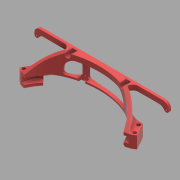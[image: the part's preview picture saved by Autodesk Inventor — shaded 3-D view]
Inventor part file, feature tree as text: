
AUTODESK INVENTOR PART (.ipt)
format: ipt  version: 2017 (Build 210142000, 142)  size: 909,824 bytes
history: native  units: mm
features: sketch x17, extrude x13, projected_geometry x12, other x8, fillet x8, plane x5, hole x4, chamfer x3, reference x3, mirror x2
ambient origin geometry x8: Origin, YZ Plane, XZ Plane, XY Plane, X Axis, Y Axis, Z Axis, Center Point
bodies: Body1 (feature_tree), Body2 (feature_tree), Body3 (feature_tree)
feature tree (75):
  other  "core"
  extrude  "Extrusion1"  Depth=12.0mm
  extrude  "Extrusion2"  Depth=18.0mm
  extrude  "Extrusion3"  Depth=17.453293mm
  chamfer  "Chamfer1"  Distance=5.0mm
  hole  "Hole1"  [1 undecoded]
  hole  "Hole2"  [1 undecoded]
  plane  "Work Plane1"
  extrude  "Extrusion4"  Depth=4.0mm
  extrude  "Extrusion5"  Depth=24.0mm TaperAngle=0.0deg
  extrude  "Extrusion6"  Depth=10.0mm
  extrude  "Extrusion11"  Depth=4.0mm TaperAngle=0.0deg
  mirror  "Mirror1"
  extrude  "Extrusion13"  Depth=0.65mm TaperAngle=45.0deg
  chamfer  "Chamfer4"  Distance=0.65mm
  plane  "Work Plane3"
  mirror  "Mirror2"
  fillet  "Fillet2"  Radius=17.0mm
  chamfer  "Chamfer3"  Distance=8.0mm
  plane  "Work Plane4"
  extrude  "Extrusion14"  Depth=4.0mm
  fillet  "Fillet3"  Radius=12.0mm
  fillet  "Fillet4"  Radius=3.0mm
  fillet  "Fillet5"  Radius=68.5mm
  plane  "Work Plane5"
  extrude  "Extrusion15"  Depth=1.6mm
  extrude  "Extrusion16"  Depth=1.6mm
  fillet  "Fillet6"  Radius=1.8mm
  fillet  "Fillet7"  Radius=1.8mm
  hole  "Hole6"  [1 undecoded]
  fillet  "Fillet8"  Radius=5.0mm
  hole  "Hole7"  [1 undecoded]
  plane  "Work Plane6"
  extrude  "Extrusion17"  TaperAngle=45.0deg  [1 undecoded]
  fillet  "Fillet9"  Radius=19.5mm
  extrude  "Extrusion18"  Depth=1.6mm
  sketch  "Sketch1"  dims[d1=8.0mm d2=12.0mm]
  reference  "Reference1"
  reference  "Reference2"
  sketch  "Sketch2"  dims[d3=3.0mm d4=0.0mm d5=18.0mm]
  projected_geometry  "Projected Loop1"
  sketch  "Sketch3"  dims[d6=6.5mm d7=0.0mm d8=17.453293mm]
  projected_geometry  "Projected Loop2"
  other  "clamp_r"
  sketch  "Sketch4"  dims[d9=16.0mm]
  projected_geometry  "Projected Loop3"
  sketch  "Sketch5"  dims[d10=6.0mm d11=5.0mm d12=0.0mm]
  sketch  "Sketch6"  dims[d13=1.5mm d14=2.0mm d15=45.0deg d19=12.0mm]
  reference  "Reference3"
  projected_geometry  "Projected Loop4"
  sketch  "Sketch7"  dims[d20=4.0mm d21=3.0mm]
  projected_geometry  "Projected Loop5"
  sketch  "Sketch8"  dims[d22=3.0mm]
  other  "Pattern of core:1"
  other  "clamp_l"
  sketch  "Sketch15"  dims[d23=2.2mm d24=6.0mm d25=4.0mm d26=2.0mm d27=90.0deg d28=8.0mm d29=20.594885mm]
  projected_geometry  "Projected Loop10"
  sketch  "Sketch17"  dims[d30=2.2mm d31=6.0mm d32=4.0mm d33=2.0mm d34=90.0deg d35=8.0mm d36=20.594885mm d38=4.0mm]
  projected_geometry  "Projected Loop12"
  sketch  "Sketch18"  dims[d39=3.0mm d40=0.0mm d41=24.0mm d42=0.0mm]
  sketch  "Sketch19"  dims[d43=10.0mm d44=0.0mm d89=4.05mm]
  sketch  "Sketch20"  dims[d90=4.05mm d91=4.0mm d92=0.0mm]
  projected_geometry  "Projected Loop13"
  projected_geometry  "Projected Loop14"
  sketch  "Sketch21"  dims[d94=4.0mm d95=2.0mm d96=2.0mm d97=45.0deg d100=0.65mm d101=0.0mm]
  projected_geometry  "Projected Loop15"
  projected_geometry  "Projected Loop16"
  sketch  "Sketch22"  dims[d102=1.2mm d103=2.0mm d104=45.0deg d106=17.0mm d107=8.0mm d108=0.0mm]
  projected_geometry  "Projected Loop18"
  sketch  "Sketch23"  dims[d109=2.0mm d110=4.0mm d111=12.0mm d112=3.0mm d113=68.5mm]
  sketch  "Sketch24"  dims[d114=158.0mm d115=16.0mm d116=4.5mm d117=1.8mm d118=1.8mm d119=1.8mm d120=5.0mm d121=5.0mm d122=45.0deg d123=45.0deg d124=19.5mm d125=1.8mm d126=6.0mm d128=3.0mm d129=0.0mm d130=3.0mm d131=0.0mm d132=3.0mm d133=6.5mm d135=1.5mm d136=6.0mm d137=4.0mm d138=2.0mm d139=90.0deg d140=8.0mm d141=20.594885mm d142=2.3mm d143=6.5mm d144=3.0mm d145=2.5mm d146=64.0mm d147=2.2mm d148=6.0mm d149=4.0mm d150=2.0mm d151=90.0deg d152=8.0mm d153=20.594885mm d154=54.75mm d155=5.0mm d156=5.0mm d157=8.0mm d158=11.0mm d159=0.0mm d160=1.5mm d161=4.0mm d162=4.0mm d163=4.0mm d164=1.6mm d165=0.0mm]
  other  "<userpath>\Dropbox\Work\HeadSLAM\xtion_custom_assembly.iam"
  other  "xtion_custom_assembly.iam"
  other  "pupil_frame_full:1"
  other  "<userpath>\Dropbox\Work\HeadSLAM\xtion_custom_assembly.iam"
note: 5 required parameter values undecoded (feature->parameter linkage not recoverable at this tier; creation-order binding heuristic only, values carry confidence <= 0.55)
